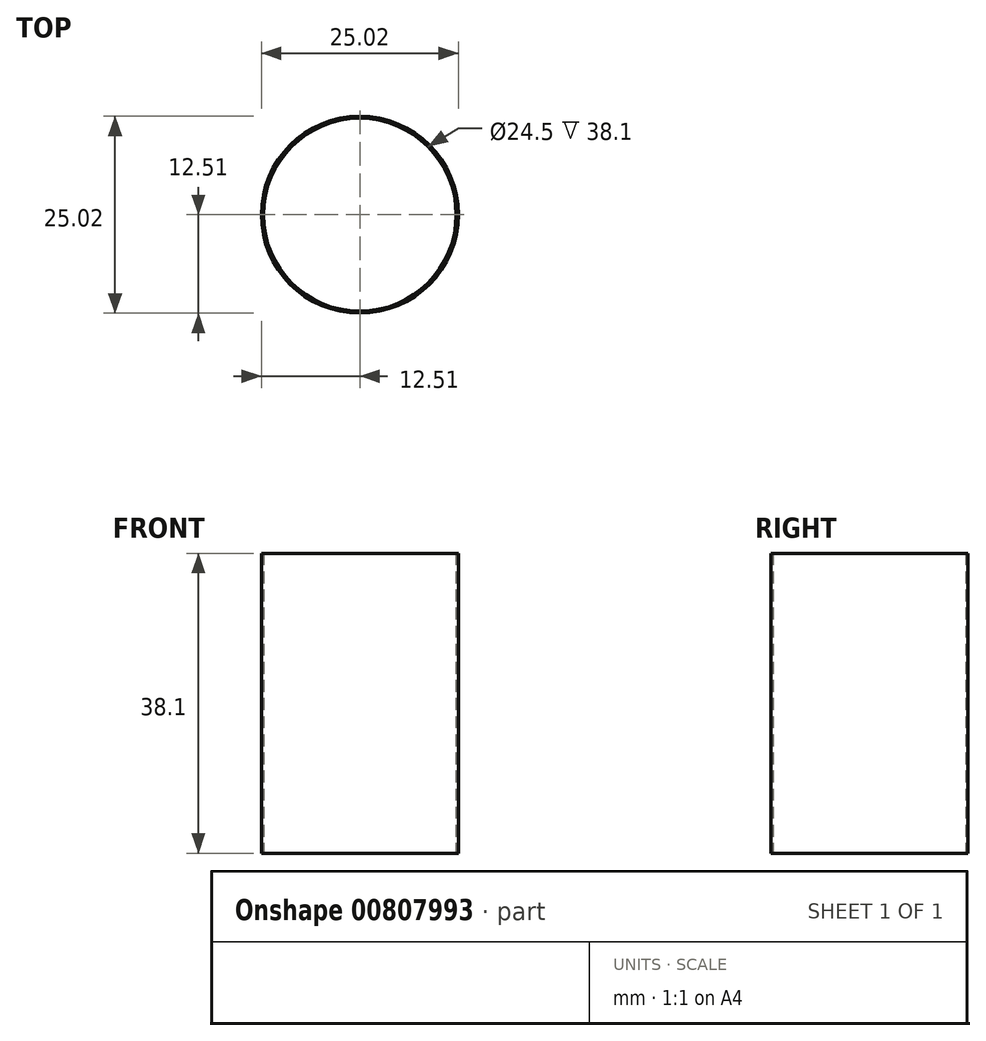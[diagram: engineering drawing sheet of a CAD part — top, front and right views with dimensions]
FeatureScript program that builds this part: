
annotation { "Feature Type Name" : "Feature", "Feature Type Description" : "" }
export const myFeature = defineFeature(function(context is Context, id is Id, definition is map)
    precondition{}
    {
        {
            var Q0;
            Q0=qCreatedBy(makeId("Top.planeOp"),FACE);
            var sketch = newSketch(context, id + "F0", { "sketchPlane" : qUnion([Q0])});
            skCircle(sketch, "E0", {"center": v(0, 0) * mm, "radius": 12.5 * mm});
            skCircle(sketch, "E1", {"center": v(0, 0) * mm, "radius": 12.25 * mm});
            skSolve(sketch);
        }
        {
            var Q0;
            Q0 = qSketchRegion(id + "F0", true);
            extrude(context, id + "F1", {"entities" : qUnion([Q0]), "depth" : 38.1 * mm, "offsetDistance" : 25.4 * mm});
        }
    });
